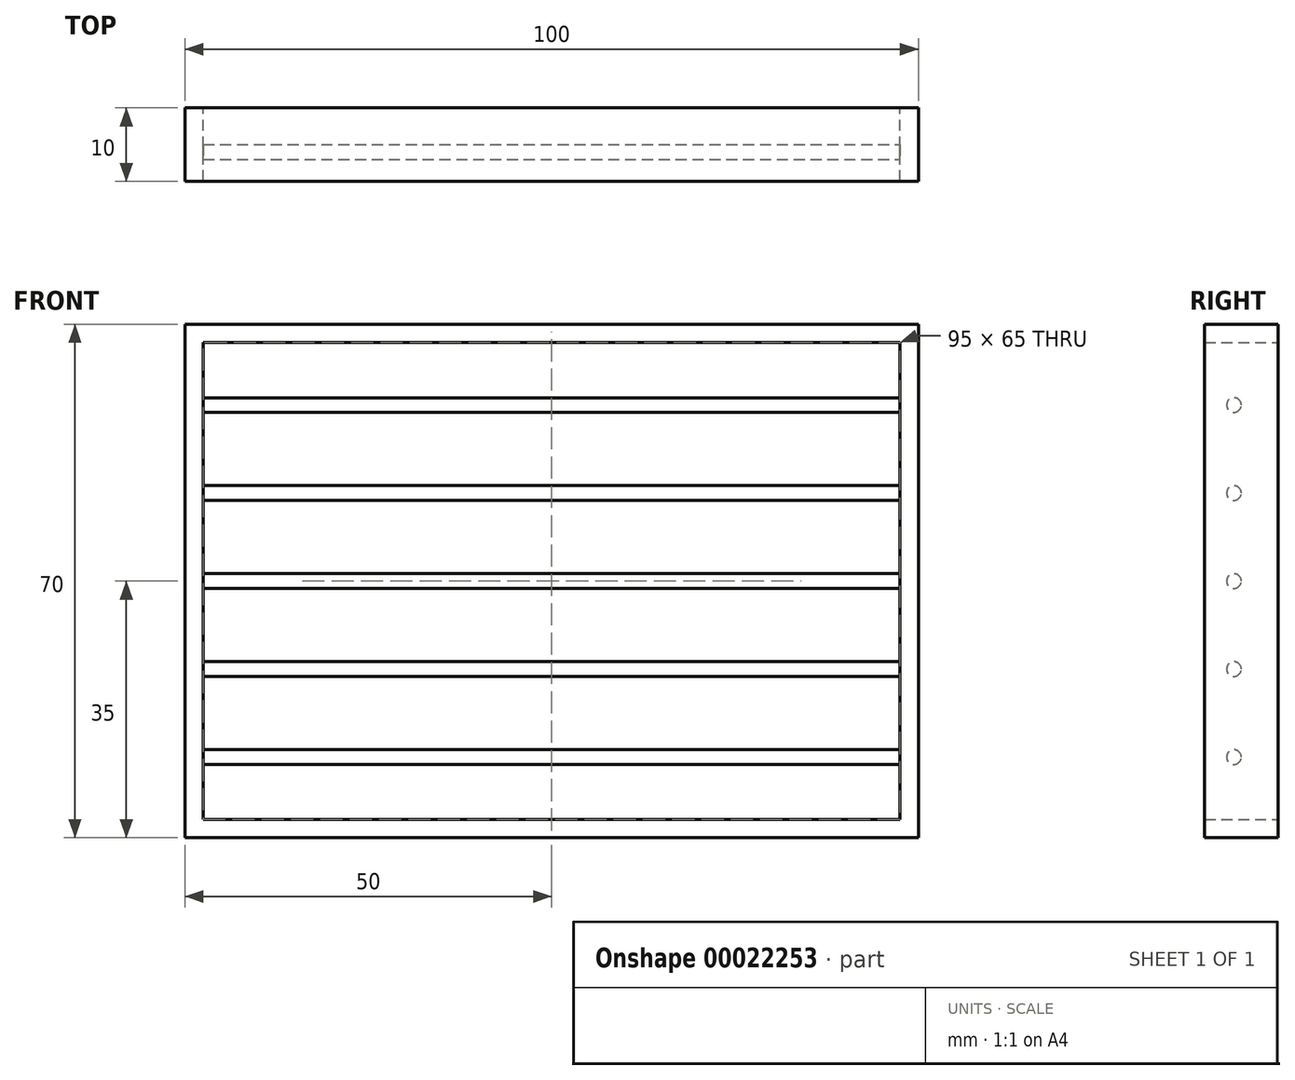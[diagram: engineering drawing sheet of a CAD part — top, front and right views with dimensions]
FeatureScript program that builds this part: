
annotation { "Feature Type Name" : "Feature", "Feature Type Description" : "" }
export const myFeature = defineFeature(function(context is Context, id is Id, definition is map)
    precondition{}
    {
        {
            var Q0;
            Q0=qCreatedBy(makeId("Front.planeOp"),FACE);
            var sketch = newSketch(context, id + "F0", { "sketchPlane" : qUnion([Q0])});
            skLineSegment(sketch, "E0.rect.bottom", {"start": v(50, -35) * mm, "end": v(-50, -35) * mm});
            skLineSegment(sketch, "E0.rect.top", {"start": v(50, 35) * mm, "end": v(-50, 35) * mm});
            skLineSegment(sketch, "E0.rect.left", {"start": v(50, -35) * mm, "end": v(50, 35) * mm});
            skLineSegment(sketch, "E0.rect.right", {"start": v(-50, -35) * mm, "end": v(-50, 35) * mm});
            skPoint(sketch, "E0.rect.middle", {"position": v(0, 0) * mm});
            skLineSegment(sketch, "E1.rect.bottom", {"start": v(47.5, -32.5) * mm, "end": v(-47.5, -32.5) * mm});
            skLineSegment(sketch, "E1.rect.top", {"start": v(47.5, 32.5) * mm, "end": v(-47.5, 32.5) * mm});
            skLineSegment(sketch, "E1.rect.left", {"start": v(47.5, -32.5) * mm, "end": v(47.5, 32.5) * mm});
            skLineSegment(sketch, "E1.rect.right", {"start": v(-47.5, -32.5) * mm, "end": v(-47.5, 32.5) * mm});
            skSolve(sketch);
        }
        {
            var Q0;
            Q0 = qSketchRegion(id + "F0", true);
            extrude(context, id + "F1", {"entities" : qUnion([Q0]), "depth" : 10 * mm});
        }
        {
            var Q0;
            Q0=makeQuery(id+"F1.opExtrude","SWEPT_FACE",FACE,{"disambiguationData":[OSD([sQuery(id+"F0.wireOp",EDGE,"E1.rect.left")])]});
            var sketch = newSketch(context, id + "F2", { "sketchPlane" : qUnion([Q0])});
            skCircle(sketch, "E2", {"center": v(6, 0) * mm, "radius": 1 * mm});
            skCircle(sketch, "E3.0.1.0", {"center": v(6, 12) * mm, "radius": 1 * mm});
            skCircle(sketch, "E3.0.2.0", {"center": v(6, 24) * mm, "radius": 1 * mm});
            skLineSegment(sketch, "E3.direction1", {"start": v(6, 0) * mm, "end": v(31, 0) * mm, "construction": true});
            skLineSegment(sketch, "E3.direction2", {"start": v(6, 0) * mm, "end": v(6, 12) * mm, "construction": true});
            skCircle(sketch, "E4.0.1.0", {"center": v(6, -12) * mm, "radius": 1 * mm});
            skCircle(sketch, "E4.0.2.0", {"center": v(6, -24) * mm, "radius": 1 * mm});
            skLineSegment(sketch, "E4.direction2", {"start": v(6, 0) * mm, "end": v(6, -12) * mm, "construction": true});
            skSolve(sketch);
        }
        {
            var Q0;
            Q0 = qSketchRegion(id + "F2", true);
            extrude(context, id + "F3", {"entities" : qUnion([Q0]), "operationType" : NewBodyOperationType.ADD, "depth" : 95 * mm});
        }
    });
